# Revit family: PRD_AR_FlshCntrlDvcs_F3SWcFlushValve_F3SF4002
name_source: partatom
category: Plumbing Fixtures
units: mm (PartAtom-declared; Revit-internal decimal feet)

## family parameters
Cut with Voids When Loaded = Yes
Enable Cutting in Views = Yes
Host = Face
Maintain Annotation Orientation = No
OmniClass Number = 23.45.55.11
OmniClass Title = Sanitary Components
Part Type = Normal
Room Calculation Point = No
Round Connector Dimension = Use Diameter
Shared = No

## types (1)
- F3SF4002
    AssetType = Fixed
    BIMObjectName = PRD_AR_FlushControlDevices_F3SWcFlushValve_F3SF4002
    BasicColour = Stainless steel-look
    BodyMaterial = PRD_AR_StainlessSteel_Brushed
    BuiltInFittingModel = Finishing section
    ButtonMaterial = PRD_AR_ChromatedBrass_HighPolished
    CW Connection = Yes
    CWFU = 0
    CalculationFlowRateColdWater = 1 l/s
    Category = Pr_75_50_46_31, Flush control devices
    CloseOffRating = 0.0 Pa
    Color = Stainless steel-look
    CoverPlateHeight = 245 mm
    CoverPlateWidth = 190 mm
    Default Elevation = 1219 mm
    Description = F3S WC flush valve DN 20 as a finished installation kit for in-wall installation in the basic installation kit, for wall-mounted toilet bowls, fitting group 1. Especially suitable for facilities at risk of vandalism. Self-closing upper component hydraulically controlled, piston-free design, automatic and backlash-free closing. Automatic flush flow regulation and adjustable flush water volume. All-metal construction, visible parts polished chromium-plated. Stainless steel cover plate 190 x 245 x 2 mm, mounting from the front with safety screws, pre-mounted push-button actuation. Hydraulic control lines and mounting material. Depth adjustability 20 mm.
    DiameterNominal = DN 20
    Export Type to IFC As = IfcValveType
    Features = All-metal construction, visible parts polished chromium-plated. Stainless steel cover plate 190 x 245 x 2 mm.
    Finish = Satin finished
    FlowCoefficient = 1 l/s
    FlushingRate = 1.3 L/s
    FlushingVolumeAdjustable = Yes
    FunctionalPrinciple = Hydraulic self-closing
    HW Connection = Yes
    HWFU = 0
    IfcExportAs = IfcValveType
    IfcExportType = FLUSHING
    IsHighPressure = No
    Manufacturer = KWC Group Management AG
    ManufacturerName = KWC Group Management AG
    ManufacturerURL = www.kwc-professional.com
    Material = Stainless steel
    MaterialCasing = Stainless steel
    MaterialCodeCasing = 1.4301 Chrome Nickel steel V2A
    MaterialFitting = brass-look
    MaximumFlowPressure = 4 bar
    MaximumFlushingFlow = 1.3 l/s
    MinimumFlowPressure = 1.2 bar
    MinimumFlushingFlow = 1 l/s
    Model = F3SF4002
    ModelNumber = 2030068201
    ModelReference = F3SF4002
    NBSDescription = Flush control devices
    NBSReference = 90-15-35/470
    Name = F3S WC flush valve F3SF4002
    NominalDepth = 2 mm  [stored 0.00656168 ft]
    NominalHeight = 245 mm  [stored 0.803806 ft]
    NominalWidth = 190 mm
    Parameterization = Manual
    ProductInformation = http://pim.kwc.com
    ProtectiveShutdown = No
    Size = 20
    SoundInsulation = No
    Status = New
    SurfaceFinishCasing = Satin finished
    SurfaceFinishFitting = Raw
    TestPressure = 0.0 Pa
    Type IFC Predefined Type = FLUSHING
    TypeOfFlushingFitting = WC flush valve
    TypeOfMounting = in-wall installation with box
    TypeOfOperation = Manual operation
    URL = www.kwc-professional.com
    Uniclass2015Code = Pr_75_50_46_31
    Uniclass2015Title = Flush control devices
    Uniclass2015Version = Products v1.36
    ValveMechanism = OTHER
    ValveOperation = HYDRAULIC
    ValvePattern = OTHER
    Vent Connection = Yes
    Version = 1
    WFU = 0
    Waste Connection = Yes
    WaterConnection = Threaded connection (external)
    WorkingPressure = 0.0 Pa

note: [stored X ft] marks values corroborated as IEEE doubles in the binary element streams (Revit-internal decimal feet)

## geometry (parser evidence)
native form markers: Sweep x7
no freeform markers — native parametric forms only
